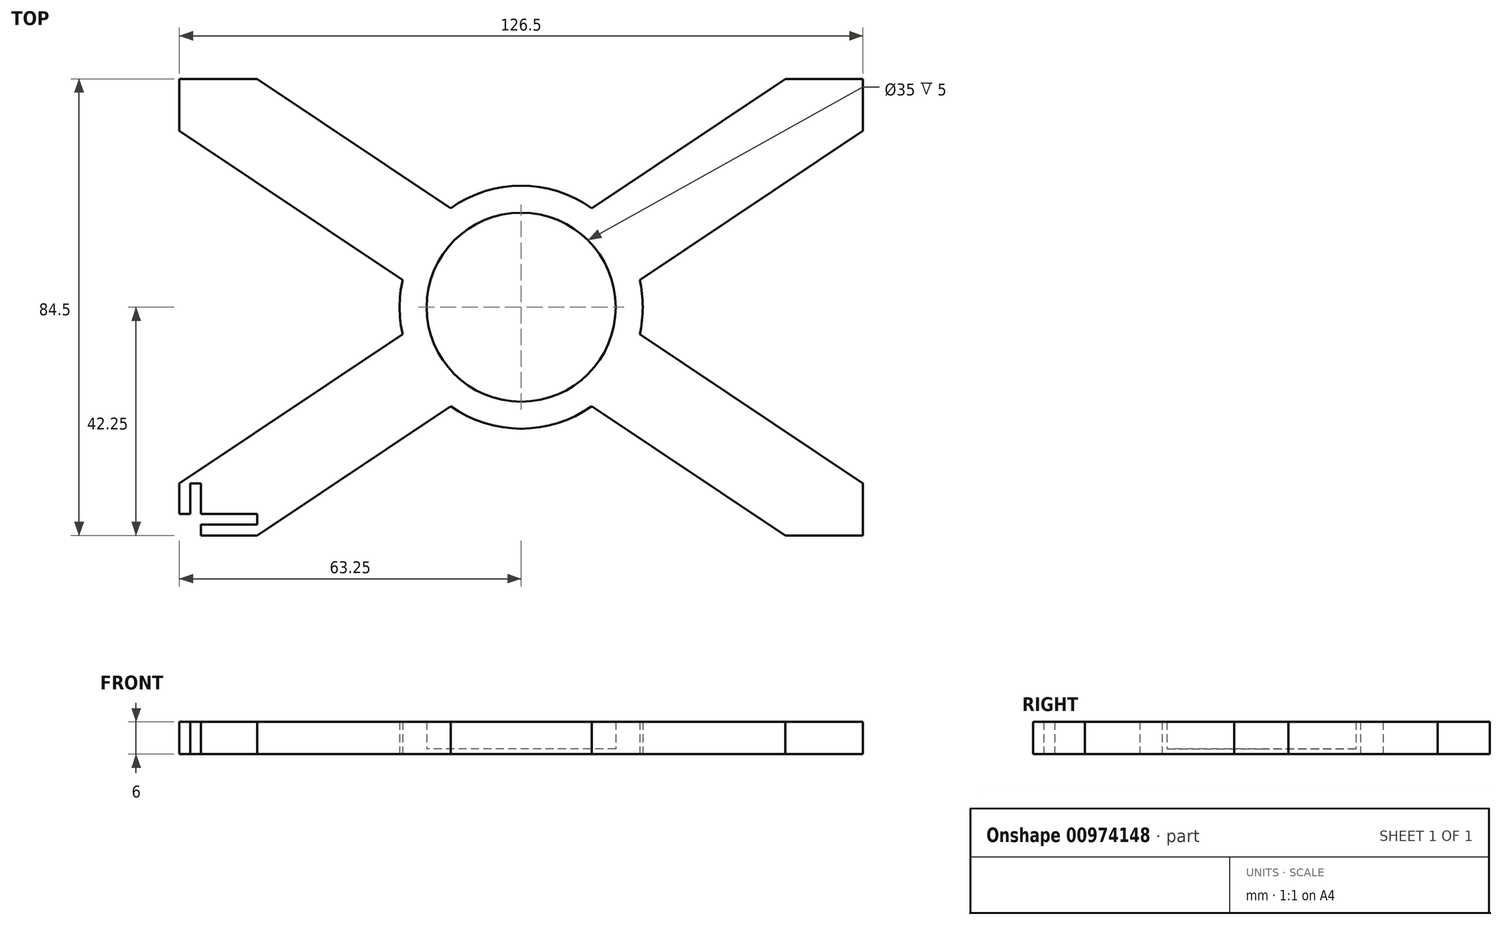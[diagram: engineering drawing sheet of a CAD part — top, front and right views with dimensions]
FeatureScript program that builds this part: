
annotation { "Feature Type Name" : "Feature", "Feature Type Description" : "" }
export const myFeature = defineFeature(function(context is Context, id is Id, definition is map)
    precondition{}
    {
        {
            var Q0;
            Q0=qCreatedBy(makeId("Top.planeOp"),FACE);
            var sketch = newSketch(context, id + "F0", { "sketchPlane" : qUnion([Q0])});
            skLineSegment(sketch, "E0.bottom", {"start": v(-63.25, -42.25) * mm, "end": v(63.25, -42.25) * mm});
            skLineSegment(sketch, "E0.top", {"start": v(-63.25, 42.25) * mm, "end": v(63.25, 42.25) * mm});
            skLineSegment(sketch, "E0.left", {"start": v(-63.25, -42.25) * mm, "end": v(-63.25, 42.25) * mm});
            skLineSegment(sketch, "E0.right", {"start": v(63.25, -42.25) * mm, "end": v(63.25, 42.25) * mm});
            skPoint(sketch, "E0.middle", {"position": v(0, 0) * mm});
            skCircle(sketch, "E1", {"center": v(0, 0) * mm, "radius": 17.5 * mm});
            skLineSegment(sketch, "E2.0", {"start": v(48.85, 42.25) * mm, "end": v(13.04, 18.33) * mm});
            skLineSegment(sketch, "E3.0", {"start": v(63.25, 32.63) * mm, "end": v(21.93, 5.03) * mm});
            skLineSegment(sketch, "E4.0", {"start": v(-63.25, 32.63) * mm, "end": v(-21.93, 5.03) * mm});
            skLineSegment(sketch, "E5.0", {"start": v(-48.85, 42.25) * mm, "end": v(-13.04, 18.33) * mm});
            skLineSegment(sketch, "E6.trimOffspring", {"start": v(-21.93, -5.03) * mm, "end": v(-63.25, -32.63) * mm});
            skLineSegment(sketch, "E7.trimOffspring", {"start": v(-13.04, -18.33) * mm, "end": v(-48.85, -42.25) * mm});
            skLineSegment(sketch, "E8.trimOffspring", {"start": v(21.93, -5.03) * mm, "end": v(63.25, -32.63) * mm});
            skLineSegment(sketch, "E9.trimOffspring", {"start": v(13.04, -18.33) * mm, "end": v(48.85, -42.25) * mm});
            skArc(sketch, "E10", {"start": v(-21.93, 5.03) * mm, "mid": v(-22.5, 0) * mm, "end": v(-21.93, -5.03) * mm});
            skArc(sketch, "E11.trimOffspring", {"start": v(-13.04, -18.33) * mm, "mid": v(0, -22.5) * mm, "end": v(13.04, -18.33) * mm});
            skArc(sketch, "E12.trimOffspring", {"start": v(21.93, -5.03) * mm, "mid": v(22.5, 0) * mm, "end": v(21.93, 5.03) * mm});
            skArc(sketch, "E13.trimOffspring", {"start": v(13.04, 18.33) * mm, "mid": v(0, 22.5) * mm, "end": v(-13.04, 18.33) * mm});
            skLineSegment(sketch, "E14", {"start": v(-48.85, -42.25) * mm, "end": v(-63.25, -42.25) * mm});
            skLineSegment(sketch, "E15", {"start": v(-63.25, -32.63) * mm, "end": v(-63.25, -42.25) * mm});
            skLineSegment(sketch, "E16.0", {"start": v(-48.85, -40.25) * mm, "end": v(-63.25, -40.25) * mm});
            skLineSegment(sketch, "E17.0", {"start": v(-61.25, -32.63) * mm, "end": v(-61.25, -42.25) * mm});
            skLineSegment(sketch, "E18.0", {"start": v(-59.25, -32.63) * mm, "end": v(-59.25, -42.25) * mm});
            skLineSegment(sketch, "E19.0", {"start": v(-48.85, -38.25) * mm, "end": v(-63.25, -38.25) * mm});
            skLineSegment(sketch, "E20", {"start": v(-59.25, -32.63) * mm, "end": v(-61.25, -32.63) * mm});
            skLineSegment(sketch, "E21", {"start": v(-48.85, -38.25) * mm, "end": v(-48.85, -40.25) * mm});
            skSolve(sketch);
        }
        {
            var Q0;
            Q0=makeQuery(id+"F0.imprint","IMPRINT",FACE,{"disambiguationData":[TD([[makeQuery(id+"F0.imprint","IMPRINT",EDGE,{"derivedFrom":sQuery(id+"F0.wireOp",EDGE,"E1")}),-1.0]])]});
            extrude(context, id + "F1", {"entities" : qUnion([Q0]), "depth" : 6 * mm, "offsetDistance" : 25 * mm});
        }
        {
            var Q0;
            Q0=makeQuery(id+"F0.imprint","IMPRINT",FACE,{"disambiguationData":[TD([[makeQuery(id+"F0.imprint","IMPRINT",EDGE,{"derivedFrom":sQuery(id+"F0.wireOp",EDGE,"E1")}),1.0]])]});
            extrude(context, id + "F2", {"entities" : qUnion([Q0]), "operationType" : NewBodyOperationType.ADD, "depth" : 1 * mm, "offsetDistance" : 25 * mm});
        }
    });
